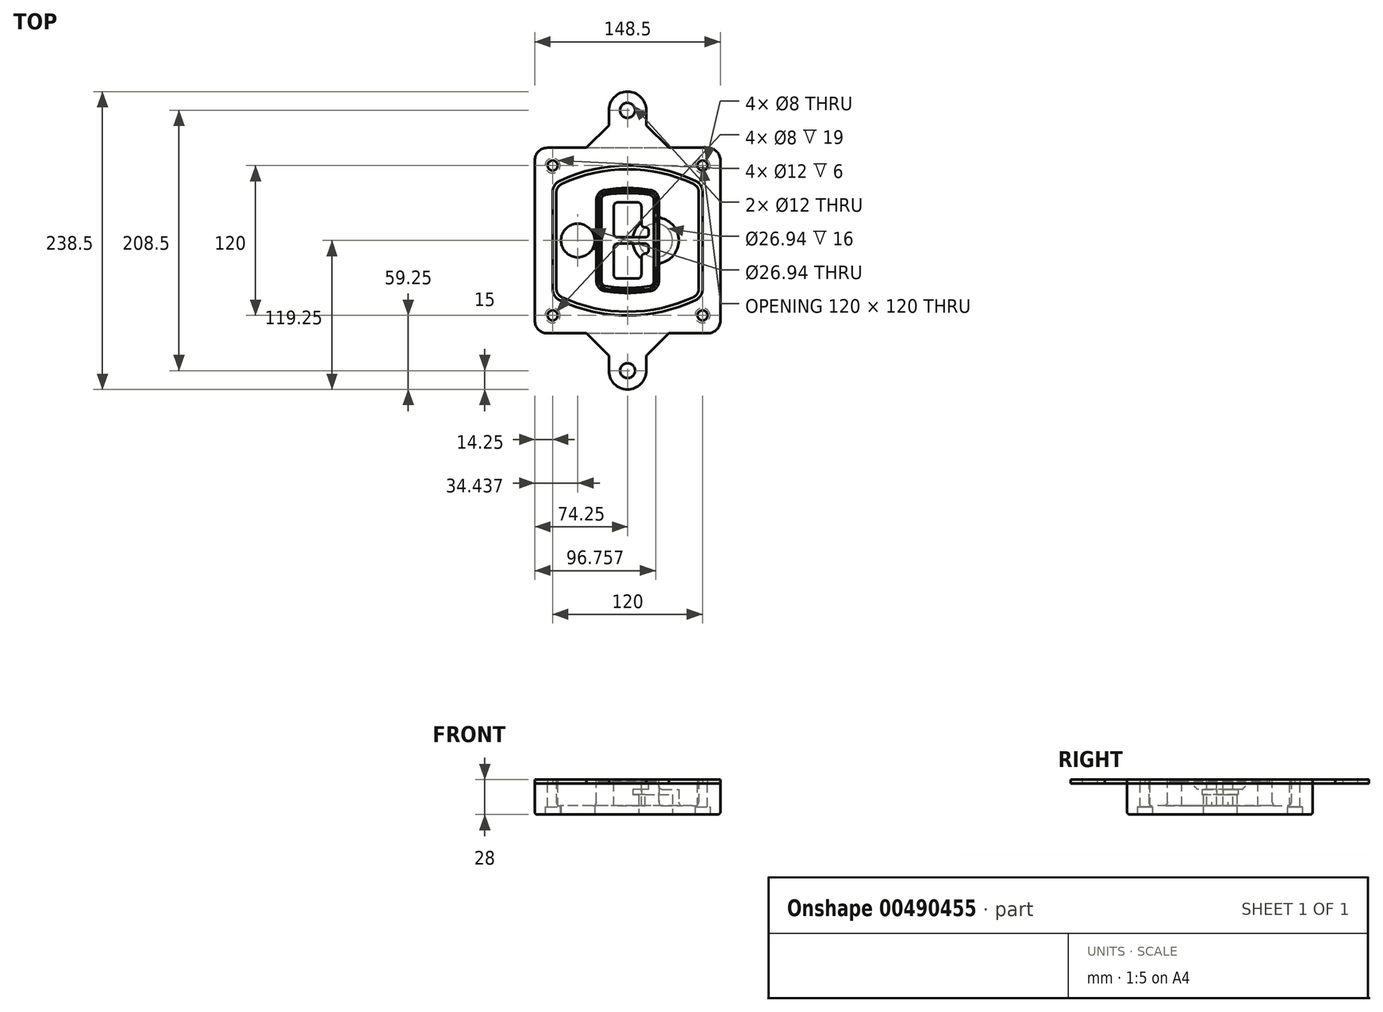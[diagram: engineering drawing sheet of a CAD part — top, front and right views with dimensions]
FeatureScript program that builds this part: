
annotation { "Feature Type Name" : "Feature", "Feature Type Description" : "" }
export const myFeature = defineFeature(function(context is Context, id is Id, definition is map)
    precondition{}
    {
        {
            var Q0;
            Q0=qCreatedBy(makeId("Top.planeOp"),FACE);
            var sketch = newSketch(context, id + "F0", { "sketchPlane" : qUnion([Q0])});
            skPoint(sketch, "E0.rect.middle", {"position": v(0, 0) * mm});
            skLineSegment(sketch, "E1.bottom", {"start": v(-64.25, -74.25) * mm, "end": v(64.25, -74.25) * mm});
            skLineSegment(sketch, "E1.top", {"start": v(-64.25, 74.25) * mm, "end": v(64.25, 74.25) * mm});
            skLineSegment(sketch, "E1.left", {"start": v(-74.25, -64.25) * mm, "end": v(-74.25, 64.25) * mm});
            skLineSegment(sketch, "E1.right", {"start": v(74.25, -64.25) * mm, "end": v(74.25, 64.25) * mm});
            skLineSegment(sketch, "E2", {"start": v(-74.25, 74.25) * mm, "end": v(74.25, -74.25) * mm, "construction": true});
            skLineSegment(sketch, "E3", {"start": v(74.25, 74.25) * mm, "end": v(-74.25, -74.25) * mm, "construction": true});
            skCircle(sketch, "E4", {"center": v(-60, 60) * mm, "radius": 4 * mm});
            skCircle(sketch, "E5", {"center": v(60, 60) * mm, "radius": 4 * mm});
            skCircle(sketch, "E6", {"center": v(60, -60) * mm, "radius": 4 * mm});
            skCircle(sketch, "E7", {"center": v(-60, -60) * mm, "radius": 4 * mm});
            skLineSegment(sketch, "E8", {"start": v(-60, 60) * mm, "end": v(60, 60) * mm, "construction": true});
            skLineSegment(sketch, "E9", {"start": v(60, 60) * mm, "end": v(60, -60) * mm, "construction": true});
            skLineSegment(sketch, "E10", {"start": v(60, -60) * mm, "end": v(-60, -60) * mm, "construction": true});
            skLineSegment(sketch, "E11", {"start": v(-60, -60) * mm, "end": v(-60, 60) * mm, "construction": true});
            skLineSegment(sketch, "E12", {"start": v(-60, 38.83) * mm, "end": v(-60, -38.83) * mm});
            skLineSegment(sketch, "E13", {"start": v(60, 38.83) * mm, "end": v(60, -38.83) * mm});
            skArc(sketch, "E14", {"start": v(54.26, 47.88) * mm, "mid": v(0, 60) * mm, "end": v(-54.26, 47.88) * mm});
            skArc(sketch, "E15", {"start": v(-54.26, -47.88) * mm, "mid": v(0, -60) * mm, "end": v(54.26, -47.88) * mm});
            skLineSegment(sketch, "E16", {"start": v(-60, 0) * mm, "end": v(60, 0) * mm, "construction": true});
            skPoint(sketch, "E17.visualSharp", {"position": v(-60, -45) * mm});
            skArc(sketch, "E17.filletArc", {"start": v(-60, -38.83) * mm, "mid": v(-58.44, -44.2) * mm, "end": v(-54.26, -47.88) * mm});
            skPoint(sketch, "E18.visualSharp", {"position": v(-60, 45) * mm});
            skArc(sketch, "E18.filletArc", {"start": v(-54.26, 47.88) * mm, "mid": v(-58.44, 44.2) * mm, "end": v(-60, 38.83) * mm});
            skPoint(sketch, "E19.visualSharp", {"position": v(60, 45) * mm});
            skArc(sketch, "E19.filletArc", {"start": v(60, 38.83) * mm, "mid": v(58.44, 44.2) * mm, "end": v(54.26, 47.88) * mm});
            skPoint(sketch, "E20.visualSharp", {"position": v(60, -45) * mm});
            skArc(sketch, "E20.filletArc", {"start": v(54.26, -47.88) * mm, "mid": v(58.44, -44.2) * mm, "end": v(60, -38.83) * mm});
            skPoint(sketch, "E21.visualSharp", {"position": v(-74.25, 74.25) * mm});
            skArc(sketch, "E21.filletArc", {"start": v(-64.25, 74.25) * mm, "mid": v(-71.32, 71.32) * mm, "end": v(-74.25, 64.25) * mm});
            skPoint(sketch, "E22.visualSharp", {"position": v(74.25, 74.25) * mm});
            skArc(sketch, "E22.filletArc", {"start": v(74.25, 64.25) * mm, "mid": v(71.32, 71.32) * mm, "end": v(64.25, 74.25) * mm});
            skPoint(sketch, "E23.visualSharp", {"position": v(74.25, -74.25) * mm});
            skArc(sketch, "E23.filletArc", {"start": v(64.25, -74.25) * mm, "mid": v(71.32, -71.32) * mm, "end": v(74.25, -64.25) * mm});
            skPoint(sketch, "E24.visualSharp", {"position": v(-74.25, -74.25) * mm});
            skArc(sketch, "E24.filletArc", {"start": v(-74.25, -64.25) * mm, "mid": v(-71.32, -71.32) * mm, "end": v(-64.25, -74.25) * mm});
            skArc(sketch, "E25.0", {"start": v(57, 38.83) * mm, "mid": v(55.9, 42.58) * mm, "end": v(52.98, 45.17) * mm});
            skLineSegment(sketch, "E25.1", {"start": v(57, 38.83) * mm, "end": v(57, -38.83) * mm});
            skArc(sketch, "E25.2", {"start": v(52.98, -45.17) * mm, "mid": v(55.9, -42.58) * mm, "end": v(57, -38.83) * mm});
            skArc(sketch, "E25.3", {"start": v(-52.98, -45.17) * mm, "mid": v(0, -57) * mm, "end": v(52.98, -45.17) * mm});
            skArc(sketch, "E25.4", {"start": v(-57, -38.83) * mm, "mid": v(-55.9, -42.58) * mm, "end": v(-52.98, -45.17) * mm});
            skArc(sketch, "E25.5", {"start": v(52.98, 45.17) * mm, "mid": v(0, 57) * mm, "end": v(-52.98, 45.17) * mm});
            skLineSegment(sketch, "E25.6", {"start": v(-57, 38.83) * mm, "end": v(-57, -38.83) * mm});
            skArc(sketch, "E25.7", {"start": v(-52.98, 45.17) * mm, "mid": v(-55.9, 42.58) * mm, "end": v(-57, 38.83) * mm});
            skArc(sketch, "E26.0", {"start": v(-55.96, 51.5) * mm, "mid": v(-61.82, 46.33) * mm, "end": v(-64, 38.83) * mm});
            skArc(sketch, "E26.1", {"start": v(55.96, 51.5) * mm, "mid": v(0, 64) * mm, "end": v(-55.96, 51.5) * mm});
            skArc(sketch, "E26.2", {"start": v(64, 38.83) * mm, "mid": v(61.82, 46.33) * mm, "end": v(55.96, 51.5) * mm});
            skLineSegment(sketch, "E26.3", {"start": v(64, 38.83) * mm, "end": v(64, -38.83) * mm});
            skArc(sketch, "E26.4", {"start": v(55.96, -51.5) * mm, "mid": v(61.82, -46.33) * mm, "end": v(64, -38.83) * mm});
            skLineSegment(sketch, "E26.5", {"start": v(-64, 38.83) * mm, "end": v(-64, -38.83) * mm});
            skArc(sketch, "E26.6", {"start": v(-55.96, -51.5) * mm, "mid": v(0, -64) * mm, "end": v(55.96, -51.5) * mm});
            skArc(sketch, "E26.7", {"start": v(-64, -38.83) * mm, "mid": v(-61.82, -46.33) * mm, "end": v(-55.96, -51.5) * mm});
            skSolve(sketch);
        }
        {
            var Q0;
            Q0=makeQuery(id+"F0.imprint","IMPRINT",FACE,{"disambiguationData":[TD([[makeQuery(id+"F0.imprint","IMPRINT",EDGE,{"derivedFrom":sQuery(id+"F0.wireOp",EDGE,"E1.bottom")}),1.0]])]});
            var Q1;
            Q1=makeQuery(id+"F0.imprint","IMPRINT",FACE,{"disambiguationData":[TD([[makeQuery(id+"F0.imprint","IMPRINT",EDGE,{"derivedFrom":sQuery(id+"F0.wireOp",EDGE,"E12")}),1.0]])]});
            var Q2;
            Q2=makeQuery(id+"F0.imprint","IMPRINT",FACE,{"disambiguationData":[TD([[makeQuery(id+"F0.imprint","IMPRINT",EDGE,{"derivedFrom":sQuery(id+"F0.wireOp",EDGE,"E25.0")}),1.0]])]});
            var Q3;
            Q3=makeQuery(id+"F0.imprint","IMPRINT",FACE,{"disambiguationData":[TD([[makeQuery(id+"F0.imprint","IMPRINT",EDGE,{"derivedFrom":sQuery(id+"F0.wireOp",EDGE,"E12")}),-1.0]])]});
            extrude(context, id + "F1", {"entities" : qUnion([Q0, Q1, Q2, Q3]), "oppositeDirection" : true, "depth" : 25 * mm});
        }
        {
            var Q0;
            Q0=makeQuery(id+"F0.imprint","IMPRINT",FACE,{"disambiguationData":[TD([[makeQuery(id+"F0.imprint","IMPRINT",EDGE,{"derivedFrom":sQuery(id+"F0.wireOp",EDGE,"E12")}),1.0]])]});
            extrude(context, id + "F2", {"entities" : qUnion([Q0]), "operationType" : NewBodyOperationType.ADD, "depth" : 3 * mm});
        }
        {
            var Q0;
            Q0=makeQuery(id+"F0.imprint","IMPRINT",FACE,{"disambiguationData":[TD([[makeQuery(id+"F0.imprint","IMPRINT",EDGE,{"derivedFrom":sQuery(id+"F0.wireOp",EDGE,"E25.0")}),1.0]])]});
            extrude(context, id + "F3", {"entities" : qUnion([Q0]), "operationType" : NewBodyOperationType.REMOVE, "oppositeDirection" : true, "depth" : 18 * mm});
        }
        {
            var Q0;
            Q0=makeQuery(id+"F2.opExtrude","CAP_FACE",FACE,{"disambiguationData":[OSD([sQuery(id+"F0.wireOp",EDGE,"E12"),sQuery(id+"F0.wireOp",EDGE,"E13"),sQuery(id+"F0.wireOp",EDGE,"E14"),sQuery(id+"F0.wireOp",EDGE,"E15"),sQuery(id+"F0.wireOp",EDGE,"E17.filletArc"),sQuery(id+"F0.wireOp",EDGE,"E18.filletArc"),sQuery(id+"F0.wireOp",EDGE,"E19.filletArc"),sQuery(id+"F0.wireOp",EDGE,"E20.filletArc"),sQuery(id+"F0.wireOp",EDGE,"E25.0"),sQuery(id+"F0.wireOp",EDGE,"E25.1"),sQuery(id+"F0.wireOp",EDGE,"E25.2"),sQuery(id+"F0.wireOp",EDGE,"E25.3"),sQuery(id+"F0.wireOp",EDGE,"E25.4"),sQuery(id+"F0.wireOp",EDGE,"E25.5"),sQuery(id+"F0.wireOp",EDGE,"E25.6"),sQuery(id+"F0.wireOp",EDGE,"E25.7")])],"isStart":false});
            var sketch = newSketch(context, id + "F4", { "sketchPlane" : qUnion([Q0])});
            skArc(sketch, "E27.0", {"start": v(-18.34, -40.45) * mm, "mid": v(0, -42) * mm, "end": v(18.34, -40.45) * mm});
            skArc(sketch, "E28.0", {"start": v(18.34, 40.45) * mm, "mid": v(0, 42) * mm, "end": v(-18.34, 40.45) * mm});
            skLineSegment(sketch, "E29", {"start": v(-25, 32.57) * mm, "end": v(-25, -32.57) * mm});
            skLineSegment(sketch, "E30", {"start": v(25, 32.57) * mm, "end": v(25, -32.57) * mm});
            skLineSegment(sketch, "E31", {"start": v(-25, 39.1) * mm, "end": v(25, 39.1) * mm, "construction": true});
            skLineSegment(sketch, "E32", {"start": v(-25, -39.1) * mm, "end": v(25, -39.1) * mm, "construction": true});
            skPoint(sketch, "E33.visualSharp", {"position": v(-25, 39.1) * mm});
            skArc(sketch, "E33.filletArc", {"start": v(-18.34, 40.45) * mm, "mid": v(-23.11, 37.73) * mm, "end": v(-25, 32.57) * mm});
            skPoint(sketch, "E34.visualSharp", {"position": v(25, 39.1) * mm});
            skArc(sketch, "E34.filletArc", {"start": v(25, 32.57) * mm, "mid": v(23.11, 37.73) * mm, "end": v(18.34, 40.45) * mm});
            skPoint(sketch, "E35.visualSharp", {"position": v(25, -39.1) * mm});
            skArc(sketch, "E35.filletArc", {"start": v(18.34, -40.45) * mm, "mid": v(23.11, -37.73) * mm, "end": v(25, -32.57) * mm});
            skPoint(sketch, "E36.visualSharp", {"position": v(-25, -39.1) * mm});
            skArc(sketch, "E36.filletArc", {"start": v(-25, -32.57) * mm, "mid": v(-23.11, -37.73) * mm, "end": v(-18.34, -40.45) * mm});
            skArc(sketch, "E37.0", {"start": v(52.98, 45.17) * mm, "mid": v(0, 57) * mm, "end": v(-52.98, 45.17) * mm});
            skArc(sketch, "E37.1", {"start": v(-52.98, 45.17) * mm, "mid": v(-55.9, 42.58) * mm, "end": v(-57, 38.83) * mm});
            skLineSegment(sketch, "E37.2", {"start": v(-57, 38.83) * mm, "end": v(-57, -38.83) * mm});
            skArc(sketch, "E37.3", {"start": v(-57, -38.83) * mm, "mid": v(-55.9, -42.58) * mm, "end": v(-52.98, -45.17) * mm});
            skArc(sketch, "E37.4", {"start": v(-52.98, -45.17) * mm, "mid": v(0, -57) * mm, "end": v(52.98, -45.17) * mm});
            skArc(sketch, "E37.5", {"start": v(52.98, -45.17) * mm, "mid": v(55.9, -42.58) * mm, "end": v(57, -38.83) * mm});
            skLineSegment(sketch, "E37.6", {"start": v(57, 38.83) * mm, "end": v(57, -38.83) * mm});
            skArc(sketch, "E37.7", {"start": v(57, 38.83) * mm, "mid": v(55.9, 42.58) * mm, "end": v(52.98, 45.17) * mm});
            skLineSegment(sketch, "E38.0", {"start": v(23, 32.57) * mm, "end": v(23, -32.57) * mm});
            skArc(sketch, "E38.1", {"start": v(18, -38.48) * mm, "mid": v(21.58, -36.44) * mm, "end": v(23, -32.57) * mm});
            skArc(sketch, "E38.2", {"start": v(-18, -38.48) * mm, "mid": v(0, -40) * mm, "end": v(18, -38.48) * mm});
            skArc(sketch, "E38.3", {"start": v(-23, -32.57) * mm, "mid": v(-21.58, -36.44) * mm, "end": v(-18, -38.48) * mm});
            skLineSegment(sketch, "E38.4", {"start": v(-23, 32.57) * mm, "end": v(-23, -32.57) * mm});
            skArc(sketch, "E38.5", {"start": v(23, 32.57) * mm, "mid": v(21.58, 36.44) * mm, "end": v(18, 38.48) * mm});
            skArc(sketch, "E38.6", {"start": v(-18, 38.48) * mm, "mid": v(-21.58, 36.44) * mm, "end": v(-23, 32.57) * mm});
            skArc(sketch, "E38.7", {"start": v(18, 38.48) * mm, "mid": v(0, 40) * mm, "end": v(-18, 38.48) * mm});
            skArc(sketch, "E39.0", {"start": v(21, 32.57) * mm, "mid": v(20.06, 35.15) * mm, "end": v(17.67, 36.5) * mm});
            skLineSegment(sketch, "E39.1", {"start": v(21, 32.57) * mm, "end": v(21, -32.57) * mm});
            skArc(sketch, "E39.2", {"start": v(17.67, -36.5) * mm, "mid": v(20.06, -35.15) * mm, "end": v(21, -32.57) * mm});
            skArc(sketch, "E39.3", {"start": v(-17.67, -36.5) * mm, "mid": v(0, -38) * mm, "end": v(17.67, -36.5) * mm});
            skArc(sketch, "E39.4", {"start": v(-21, -32.57) * mm, "mid": v(-20.06, -35.15) * mm, "end": v(-17.67, -36.5) * mm});
            skArc(sketch, "E39.5", {"start": v(17.67, 36.5) * mm, "mid": v(0, 38) * mm, "end": v(-17.67, 36.5) * mm});
            skLineSegment(sketch, "E39.6", {"start": v(-21, 32.57) * mm, "end": v(-21, -32.57) * mm});
            skArc(sketch, "E39.7", {"start": v(-17.67, 36.5) * mm, "mid": v(-20.06, 35.15) * mm, "end": v(-21, 32.57) * mm});
            skLineSegment(sketch, "E40", {"start": v(-25, 0) * mm, "end": v(25, 0) * mm, "construction": true});
            skLineSegment(sketch, "E41", {"start": v(-11, 5.5) * mm, "end": v(-11, 27.5) * mm});
            skLineSegment(sketch, "E42", {"start": v(-8, 30.5) * mm, "end": v(8, 30.5) * mm});
            skLineSegment(sketch, "E43", {"start": v(11, 27.5) * mm, "end": v(11, 13.5) * mm});
            skLineSegment(sketch, "E44", {"start": v(14, 10.5) * mm, "end": v(14, 10.5) * mm});
            skLineSegment(sketch, "E45", {"start": v(17, 7.5) * mm, "end": v(17, 5.5) * mm});
            skLineSegment(sketch, "E46", {"start": v(14, 2.5) * mm, "end": v(-8, 2.5) * mm});
            skPoint(sketch, "E47.visualSharp", {"position": v(-11, 30.5) * mm});
            skArc(sketch, "E47.filletArc", {"start": v(-8, 30.5) * mm, "mid": v(-10.12, 29.62) * mm, "end": v(-11, 27.5) * mm});
            skPoint(sketch, "E48.visualSharp", {"position": v(11, 30.5) * mm});
            skArc(sketch, "E48.filletArc", {"start": v(11, 27.5) * mm, "mid": v(10.12, 29.62) * mm, "end": v(8, 30.5) * mm});
            skPoint(sketch, "E49.visualSharp", {"position": v(11, 10.5) * mm});
            skArc(sketch, "E49.filletArc", {"start": v(11, 13.5) * mm, "mid": v(11.88, 11.38) * mm, "end": v(14, 10.5) * mm});
            skPoint(sketch, "E50.visualSharp", {"position": v(17, 10.5) * mm});
            skArc(sketch, "E50.filletArc", {"start": v(17, 7.5) * mm, "mid": v(16.12, 9.62) * mm, "end": v(14, 10.5) * mm});
            skPoint(sketch, "E51.visualSharp", {"position": v(17, 2.5) * mm});
            skArc(sketch, "E51.filletArc", {"start": v(14, 2.5) * mm, "mid": v(16.12, 3.38) * mm, "end": v(17, 5.5) * mm});
            skPoint(sketch, "E52.visualSharp", {"position": v(-11, 2.5) * mm});
            skArc(sketch, "E52.filletArc", {"start": v(-11, 5.5) * mm, "mid": v(-10.12, 3.38) * mm, "end": v(-8, 2.5) * mm});
            skLineSegment(sketch, "E53.0.MirrorCS", {"start": v(14, -2.5) * mm, "end": v(-8, -2.5) * mm});
            skArc(sketch, "E54.0.MirrorCS", {"start": v(-11, -5.5) * mm, "mid": v(-10.12, -3.38) * mm, "end": v(-8, -2.5) * mm});
            skLineSegment(sketch, "E55.0.MirrorCS", {"start": v(-11, -5.5) * mm, "end": v(-11, -27.5) * mm});
            skArc(sketch, "E56.0.MirrorCS", {"start": v(-8, -30.5) * mm, "mid": v(-10.12, -29.62) * mm, "end": v(-11, -27.5) * mm});
            skLineSegment(sketch, "E57.0.MirrorCS", {"start": v(-8, -30.5) * mm, "end": v(8, -30.5) * mm});
            skArc(sketch, "E58.0.MirrorCS", {"start": v(11, -27.5) * mm, "mid": v(10.12, -29.62) * mm, "end": v(8, -30.5) * mm});
            skLineSegment(sketch, "E59.0.MirrorCS", {"start": v(11, -27.5) * mm, "end": v(11, -13.5) * mm});
            skArc(sketch, "E60.0.MirrorCS", {"start": v(11, -13.5) * mm, "mid": v(11.88, -11.38) * mm, "end": v(14, -10.5) * mm});
            skArc(sketch, "E61.0.MirrorCS", {"start": v(17, -7.5) * mm, "mid": v(16.12, -9.62) * mm, "end": v(14, -10.5) * mm});
            skLineSegment(sketch, "E62.0.MirrorCS", {"start": v(17, -7.5) * mm, "end": v(17, -5.5) * mm});
            skArc(sketch, "E63.0.MirrorCS", {"start": v(14, -2.5) * mm, "mid": v(16.12, -3.38) * mm, "end": v(17, -5.5) * mm});
            skSolve(sketch);
        }
        {
            var Q0;
            Q0=makeQuery(id+"F4.imprint","IMPRINT",FACE,{"disambiguationData":[TD([[makeQuery(id+"F4.imprint","IMPRINT",EDGE,{"derivedFrom":sQuery(id+"F4.wireOp",EDGE,"E27.0")}),1.0]])]});
            var Q1;
            Q1=makeQuery(id+"F4.imprint","IMPRINT",FACE,{"disambiguationData":[TD([[makeQuery(id+"F4.imprint","IMPRINT",EDGE,{"derivedFrom":sQuery(id+"F4.wireOp",EDGE,"E38.0")}),-1.0]])]});
            var Q2;
            Q2=makeQuery(id+"F4.imprint","IMPRINT",FACE,{"disambiguationData":[TD([[makeQuery(id+"F4.imprint","IMPRINT",EDGE,{"derivedFrom":sQuery(id+"F4.wireOp",EDGE,"E39.0")}),1.0]])]});
            extrude(context, id + "F5", {"entities" : qUnion([Q0, Q1, Q2]), "operationType" : NewBodyOperationType.ADD, "endBound" : BoundingType.UP_TO_NEXT, "oppositeDirection" : true, "depth" : 25 * mm});
        }
        {
            var Q0;
            Q0=makeQuery(id+"F4.imprint","IMPRINT",FACE,{"disambiguationData":[TD([[makeQuery(id+"F4.imprint","IMPRINT",EDGE,{"derivedFrom":sQuery(id+"F4.wireOp",EDGE,"E38.0")}),-1.0]])]});
            extrude(context, id + "F6", {"entities" : qUnion([Q0]), "operationType" : NewBodyOperationType.REMOVE, "oppositeDirection" : true, "depth" : 2 * mm});
        }
        {
            var Q0;
            Q0=makeQuery(id+"F1.opExtrude","CAP_FACE",FACE,{"disambiguationData":[OSD([sQuery(id+"F0.wireOp",EDGE,"E1.bottom"),sQuery(id+"F0.wireOp",EDGE,"E1.top"),sQuery(id+"F0.wireOp",EDGE,"E1.left"),sQuery(id+"F0.wireOp",EDGE,"E1.right"),sQuery(id+"F0.wireOp",EDGE,"E4"),sQuery(id+"F0.wireOp",EDGE,"E5"),sQuery(id+"F0.wireOp",EDGE,"E6"),sQuery(id+"F0.wireOp",EDGE,"E7"),sQuery(id+"F0.wireOp",EDGE,"E21.filletArc"),sQuery(id+"F0.wireOp",EDGE,"E22.filletArc"),sQuery(id+"F0.wireOp",EDGE,"E23.filletArc"),sQuery(id+"F0.wireOp",EDGE,"E24.filletArc")])],"isStart":false});
            var sketch = newSketch(context, id + "F7", { "sketchPlane" : qUnion([Q0])});
            skCircle(sketch, "E64", {"center": v(22.5, 0) * mm, "radius": 13.47 * mm});
            skCircle(sketch, "E65", {"center": v(-39.81, 0) * mm, "radius": 13.47 * mm});
            skLineSegment(sketch, "E66", {"start": v(74.25, 0) * mm, "end": v(-74.25, 0) * mm});
            skCircle(sketch, "E67", {"center": v(22.5, 0) * mm, "radius": 18.47 * mm});
            skCircle(sketch, "E68", {"center": v(60, -60) * mm, "radius": 6 * mm});
            skCircle(sketch, "E69", {"center": v(-60, -60) * mm, "radius": 6 * mm});
            skCircle(sketch, "E70", {"center": v(-60, 60) * mm, "radius": 6 * mm});
            skCircle(sketch, "E71", {"center": v(60, 60) * mm, "radius": 6 * mm});
            skSolve(sketch);
        }
        {
            var Q0;
            {var subQ1=sQuery(id+"F7.wireOp",EDGE,"E66");var subQ4=sQuery(id+"F7.wireOp",EDGE,"E64");var subQ6=makeQuery(id+"F7.imprint","INTERSECT",VERTEX,{"disambiguationData":[OD(0.0)],"derivedFrom":[subQ4,subQ1]});Q0=makeQuery(id+"F7.imprint","IMPRINT",FACE,{"disambiguationData":[TD([[makeQuery(id+"F7.imprint","IMPRINT",EDGE,{"disambiguationData":[TD([[subQ6,-1.0]])],"derivedFrom":subQ4}),-1.0]])]});}
            var Q1;
            {var subQ0=sQuery(id+"F7.wireOp",EDGE,"E66");var subQ1=sQuery(id+"F7.wireOp",EDGE,"E64");var subQ3=makeQuery(id+"F7.imprint","INTERSECT",VERTEX,{"disambiguationData":[OD(0.0)],"derivedFrom":[subQ1,subQ0]});Q1=makeQuery(id+"F7.imprint","IMPRINT",FACE,{"disambiguationData":[TD([[makeQuery(id+"F7.imprint","IMPRINT",EDGE,{"disambiguationData":[TD([[subQ3,-1.0]])],"derivedFrom":subQ1}),1.0]])]});}
            var Q2;
            {var subQ0=sQuery(id+"F7.wireOp",EDGE,"E66");var subQ1=sQuery(id+"F7.wireOp",EDGE,"E64");var subQ3=makeQuery(id+"F7.imprint","INTERSECT",VERTEX,{"disambiguationData":[OD(0.0)],"derivedFrom":[subQ1,subQ0]});Q2=makeQuery(id+"F7.imprint","IMPRINT",FACE,{"disambiguationData":[TD([[makeQuery(id+"F7.imprint","IMPRINT",EDGE,{"disambiguationData":[TD([[subQ3,1.0]])],"derivedFrom":subQ1}),1.0]])]});}
            var Q3;
            {var subQ1=sQuery(id+"F7.wireOp",EDGE,"E66");var subQ4=sQuery(id+"F7.wireOp",EDGE,"E64");var subQ6=makeQuery(id+"F7.imprint","INTERSECT",VERTEX,{"disambiguationData":[OD(0.0)],"derivedFrom":[subQ4,subQ1]});Q3=makeQuery(id+"F7.imprint","IMPRINT",FACE,{"disambiguationData":[TD([[makeQuery(id+"F7.imprint","IMPRINT",EDGE,{"disambiguationData":[TD([[subQ6,1.0]])],"derivedFrom":subQ4}),-1.0]])]});}
            extrude(context, id + "F8", {"entities" : qUnion([Q0, Q1, Q2, Q3]), "operationType" : NewBodyOperationType.ADD, "oppositeDirection" : true, "depth" : 20 * mm});
        }
        {
            var Q0;
            {var subQ0=sQuery(id+"F7.wireOp",EDGE,"E66");var subQ1=sQuery(id+"F7.wireOp",EDGE,"E64");var subQ3=makeQuery(id+"F7.imprint","INTERSECT",VERTEX,{"disambiguationData":[OD(0.0)],"derivedFrom":[subQ1,subQ0]});Q0=makeQuery(id+"F7.imprint","IMPRINT",FACE,{"disambiguationData":[TD([[makeQuery(id+"F7.imprint","IMPRINT",EDGE,{"disambiguationData":[TD([[subQ3,-1.0]])],"derivedFrom":subQ1}),1.0]])]});}
            var Q1;
            {var subQ0=sQuery(id+"F7.wireOp",EDGE,"E66");var subQ1=sQuery(id+"F7.wireOp",EDGE,"E64");var subQ3=makeQuery(id+"F7.imprint","INTERSECT",VERTEX,{"disambiguationData":[OD(0.0)],"derivedFrom":[subQ1,subQ0]});Q1=makeQuery(id+"F7.imprint","IMPRINT",FACE,{"disambiguationData":[TD([[makeQuery(id+"F7.imprint","IMPRINT",EDGE,{"disambiguationData":[TD([[subQ3,1.0]])],"derivedFrom":subQ1}),1.0]])]});}
            extrude(context, id + "F9", {"entities" : qUnion([Q0, Q1]), "operationType" : NewBodyOperationType.REMOVE, "oppositeDirection" : true, "depth" : 16 * mm});
        }
        {
            var Q0;
            {var subQ0=sQuery(id+"F7.wireOp",EDGE,"E66");var subQ1=sQuery(id+"F7.wireOp",EDGE,"E65");var subQ3=makeQuery(id+"F7.imprint","INTERSECT",VERTEX,{"disambiguationData":[OD(0.0)],"derivedFrom":[subQ1,subQ0]});Q0=makeQuery(id+"F7.imprint","IMPRINT",FACE,{"disambiguationData":[TD([[makeQuery(id+"F7.imprint","IMPRINT",EDGE,{"disambiguationData":[TD([[subQ3,-1.0]])],"derivedFrom":subQ1}),1.0]])]});}
            var Q1;
            {var subQ0=sQuery(id+"F7.wireOp",EDGE,"E66");var subQ1=sQuery(id+"F7.wireOp",EDGE,"E65");var subQ3=makeQuery(id+"F7.imprint","INTERSECT",VERTEX,{"disambiguationData":[OD(0.0)],"derivedFrom":[subQ1,subQ0]});Q1=makeQuery(id+"F7.imprint","IMPRINT",FACE,{"disambiguationData":[TD([[makeQuery(id+"F7.imprint","IMPRINT",EDGE,{"disambiguationData":[TD([[subQ3,1.0]])],"derivedFrom":subQ1}),1.0]])]});}
            extrude(context, id + "F10", {"entities" : qUnion([Q0, Q1]), "operationType" : NewBodyOperationType.REMOVE, "oppositeDirection" : true, "depth" : 25 * mm});
        }
        {
            var Q0;
            Q0=makeQuery(id+"F7.imprint","IMPRINT",FACE,{"disambiguationData":[TD([[makeQuery(id+"F7.imprint","IMPRINT",EDGE,{"derivedFrom":sQuery(id+"F7.wireOp",EDGE,"E68")}),1.0]])]});
            var Q1;
            Q1=makeQuery(id+"F7.imprint","IMPRINT",FACE,{"disambiguationData":[TD([[makeQuery(id+"F7.imprint","IMPRINT",EDGE,{"derivedFrom":makeQuery(id+"F1.opExtrude","CAP_EDGE",EDGE,{"disambiguationData":[OSD([sQuery(id+"F0.wireOp",EDGE,"E5")])],"isStart":false})}),-1.0]])]});
            var Q2;
            Q2=makeQuery(id+"F7.imprint","IMPRINT",FACE,{"disambiguationData":[TD([[makeQuery(id+"F7.imprint","IMPRINT",EDGE,{"derivedFrom":sQuery(id+"F7.wireOp",EDGE,"E69")}),1.0]])]});
            var Q3;
            Q3=makeQuery(id+"F7.imprint","IMPRINT",FACE,{"disambiguationData":[TD([[makeQuery(id+"F7.imprint","IMPRINT",EDGE,{"derivedFrom":makeQuery(id+"F1.opExtrude","CAP_EDGE",EDGE,{"disambiguationData":[OSD([sQuery(id+"F0.wireOp",EDGE,"E4")])],"isStart":false})}),-1.0]])]});
            var Q4;
            Q4=makeQuery(id+"F7.imprint","IMPRINT",FACE,{"disambiguationData":[TD([[makeQuery(id+"F7.imprint","IMPRINT",EDGE,{"derivedFrom":sQuery(id+"F7.wireOp",EDGE,"E70")}),1.0]])]});
            var Q5;
            Q5=makeQuery(id+"F7.imprint","IMPRINT",FACE,{"disambiguationData":[TD([[makeQuery(id+"F7.imprint","IMPRINT",EDGE,{"derivedFrom":makeQuery(id+"F1.opExtrude","CAP_EDGE",EDGE,{"disambiguationData":[OSD([sQuery(id+"F0.wireOp",EDGE,"E7")])],"isStart":false})}),-1.0]])]});
            var Q6;
            Q6=makeQuery(id+"F7.imprint","IMPRINT",FACE,{"disambiguationData":[TD([[makeQuery(id+"F7.imprint","IMPRINT",EDGE,{"derivedFrom":sQuery(id+"F7.wireOp",EDGE,"E71")}),1.0]])]});
            var Q7;
            Q7=makeQuery(id+"F7.imprint","IMPRINT",FACE,{"disambiguationData":[TD([[makeQuery(id+"F7.imprint","IMPRINT",EDGE,{"derivedFrom":makeQuery(id+"F1.opExtrude","CAP_EDGE",EDGE,{"disambiguationData":[OSD([sQuery(id+"F0.wireOp",EDGE,"E6")])],"isStart":false})}),-1.0]])]});
            extrude(context, id + "F11", {"entities" : qUnion([Q0, Q1, Q2, Q3, Q4, Q5, Q6, Q7]), "operationType" : NewBodyOperationType.REMOVE, "oppositeDirection" : true, "depth" : 6 * mm});
        }
        {
            var Q0;
            Q0=makeQuery(id+"F9.boolean.opBoolean","COPY",FACE,{"derivedFrom":makeQuery(id+"F9.opExtrude","CAP_FACE",FACE,{"disambiguationData":[OSD([sQuery(id+"F7.wireOp",EDGE,"E64")])],"isStart":false})});
            var sketch = newSketch(context, id + "F12", { "sketchPlane" : qUnion([Q0])});
            skArc(sketch, "E72.0", {"start": v(11, 14.45) * mm, "mid": v(6.45, 9.13) * mm, "end": v(4.2, 2.5) * mm});
            skArc(sketch, "E72.1", {"start": v(4.2, -2.5) * mm, "mid": v(6.45, -9.13) * mm, "end": v(11, -14.45) * mm});
            skLineSegment(sketch, "E73", {"start": v(4.2, -2.5) * mm, "end": v(14, -2.5) * mm});
            skLineSegment(sketch, "E74.0", {"start": v(14, 2.5) * mm, "end": v(4.2, 2.5) * mm});
            skArc(sketch, "E74.1", {"start": v(14, 2.5) * mm, "mid": v(16.12, 3.38) * mm, "end": v(17, 5.5) * mm});
            skLineSegment(sketch, "E74.2", {"start": v(17, 7.5) * mm, "end": v(17, 5.5) * mm});
            skArc(sketch, "E74.3", {"start": v(17, 7.5) * mm, "mid": v(16.12, 9.62) * mm, "end": v(14, 10.5) * mm});
            skArc(sketch, "E74.4", {"start": v(11, 13.5) * mm, "mid": v(11.88, 11.38) * mm, "end": v(14, 10.5) * mm});
            skLineSegment(sketch, "E74.5", {"start": v(11, 14.45) * mm, "end": v(11, 13.5) * mm});
            skLineSegment(sketch, "E74.7", {"start": v(14, -2.5) * mm, "end": v(4.2, -2.5) * mm});
            skArc(sketch, "E74.8", {"start": v(14, -2.5) * mm, "mid": v(16.12, -3.38) * mm, "end": v(17, -5.5) * mm});
            skLineSegment(sketch, "E74.9", {"start": v(17, -7.5) * mm, "end": v(17, -5.5) * mm});
            skArc(sketch, "E74.10", {"start": v(17, -7.5) * mm, "mid": v(16.12, -9.62) * mm, "end": v(14, -10.5) * mm});
            skArc(sketch, "E74.11", {"start": v(11, -13.5) * mm, "mid": v(11.88, -11.38) * mm, "end": v(14, -10.5) * mm});
            skLineSegment(sketch, "E74.12", {"start": v(11, -14.45) * mm, "end": v(11, -13.5) * mm});
            skPoint(sketch, "E75.orphan", {"position": v(11, -27.5) * mm});
            skPoint(sketch, "E76.orphan", {"position": v(-8, -2.5) * mm});
            skPoint(sketch, "E77.orphan", {"position": v(-8, 2.5) * mm});
            skPoint(sketch, "E78.orphan", {"position": v(11, 27.5) * mm});
            skSolve(sketch);
        }
        {
            var Q0;
            {var subQ7=sQuery(id+"F12.wireOp",EDGE,"E72.0");var subQ14=sQuery(id+"F12.wireOp",EDGE,"E72.1");var subQ16=sQuery(id+"F12.wireOp",EDGE,"E74.1");var subQ18=sQuery(id+"F12.wireOp",EDGE,"E74.8");Q0=qUnion([makeQuery(id+"F12.imprint","IMPRINT",FACE,{"disambiguationData":[TD([[makeQuery(id+"F12.imprint","IMPRINT",EDGE,{"derivedFrom":subQ7}),1.0]])]}),makeQuery(id+"F12.imprint","IMPRINT",FACE,{"disambiguationData":[TD([[makeQuery(id+"F12.imprint","IMPRINT",EDGE,{"derivedFrom":subQ14}),1.0]])]}),makeQuery(id+"F12.imprint","IMPRINT",FACE,{"disambiguationData":[TD([[makeQuery(id+"F12.imprint","IMPRINT",EDGE,{"derivedFrom":subQ16}),1.0]])]}),makeQuery(id+"F12.imprint","IMPRINT",FACE,{"disambiguationData":[TD([[makeQuery(id+"F12.imprint","IMPRINT",EDGE,{"derivedFrom":subQ18}),-1.0]])]})]);}
            var Q1;
            Q1=makeQuery(id+"F5.boolean.opBoolean","SPLIT",FACE,{"disambiguationData":[TD([makeQuery(id+"F5.opExtrude","SWEPT_FACE",FACE,{"disambiguationData":[OSD([sQuery(id+"F4.wireOp",EDGE,"E41")])]})])],"derivedFrom":makeQuery(id+"F3.boolean.opBoolean","COPY",FACE,{"derivedFrom":makeQuery(id+"F3.opExtrude","CAP_FACE",FACE,{"disambiguationData":[OSD([sQuery(id+"F0.wireOp",EDGE,"E25.0"),sQuery(id+"F0.wireOp",EDGE,"E25.1"),sQuery(id+"F0.wireOp",EDGE,"E25.2"),sQuery(id+"F0.wireOp",EDGE,"E25.3"),sQuery(id+"F0.wireOp",EDGE,"E25.4"),sQuery(id+"F0.wireOp",EDGE,"E25.5"),sQuery(id+"F0.wireOp",EDGE,"E25.6"),sQuery(id+"F0.wireOp",EDGE,"E25.7")])],"isStart":false})})});
            extrude(context, id + "F13", {"entities" : qUnion([Q0]), "operationType" : NewBodyOperationType.REMOVE, "endBound" : BoundingType.UP_TO_SURFACE, "endBoundEntityFace" : qUnion([Q1]), "depth" : 25 * mm});
        }
        {
            var Q0;
            Q0=makeQuery(id+"F3.boolean.opBoolean","COPY",EDGE,{"derivedFrom":makeQuery(id+"F3.opExtrude","CAP_EDGE",EDGE,{"disambiguationData":[OSD([sQuery(id+"F0.wireOp",EDGE,"E25.6")])],"isStart":false})});
            var Q1;
            Q1=makeQuery(id+"F8.boolean.opBoolean","INTERSECT",EDGE,{"derivedFrom":[makeQuery(id+"F5.opExtrude","SWEPT_FACE",FACE,{"disambiguationData":[OSD([sQuery(id+"F4.wireOp",EDGE,"E30")])]}),makeQuery(id+"F8.opExtrude","CAP_FACE",FACE,{"disambiguationData":[OSD([sQuery(id+"F7.wireOp",EDGE,"E67")])],"isStart":false})]});
            var Q2;
            Q2=makeQuery(id+"F8.boolean.opBoolean","INTERSECT",EDGE,{"disambiguationData":[OD(1.0)],"derivedFrom":[makeQuery(id+"F5.opExtrude","SWEPT_FACE",FACE,{"disambiguationData":[OSD([sQuery(id+"F4.wireOp",EDGE,"E30")])]}),makeQuery(id+"F8.opExtrude","SWEPT_FACE",FACE,{"disambiguationData":[OSD([sQuery(id+"F7.wireOp",EDGE,"E67")])]})]});
            var Q3;
            {var subQ0=sQuery(id+"F4.wireOp",EDGE,"E30");Q3=makeQuery(id+"F8.boolean.opBoolean","SPLIT",EDGE,{"disambiguationData":[TD([makeQuery(id+"F5.opExtrude","SWEPT_FACE",FACE,{"disambiguationData":[OSD([sQuery(id+"F4.wireOp",EDGE,"E35.filletArc")])]})])],"derivedFrom":makeQuery(id+"F5.opExtrude","CAP_EDGE",EDGE,{"disambiguationData":[OSD([subQ0])],"isStart":false})});}
            var Q4;
            {var subQ0=sQuery(id+"F0.wireOp",EDGE,"E25.7");var subQ1=sQuery(id+"F0.wireOp",EDGE,"E25.1");var subQ2=sQuery(id+"F0.wireOp",EDGE,"E25.6");var subQ3=sQuery(id+"F0.wireOp",EDGE,"E25.5");var subQ4=sQuery(id+"F0.wireOp",EDGE,"E25.4");var subQ5=sQuery(id+"F0.wireOp",EDGE,"E25.0");var subQ6=sQuery(id+"F0.wireOp",EDGE,"E25.2");var subQ7=sQuery(id+"F0.wireOp",EDGE,"E25.3");Q4=makeQuery(id+"F8.boolean.opBoolean","INTERSECT",EDGE,{"derivedFrom":[makeQuery(id+"F5.boolean.opBoolean","SPLIT",FACE,{"disambiguationData":[TD([makeQuery(id+"F2.opExtrude","SWEPT_FACE",FACE,{"disambiguationData":[OSD([subQ5])]})])],"derivedFrom":makeQuery(id+"F3.boolean.opBoolean","COPY",FACE,{"derivedFrom":makeQuery(id+"F3.opExtrude","CAP_FACE",FACE,{"disambiguationData":[OSD([subQ5,subQ1,subQ6,subQ7,subQ4,subQ3,subQ2,subQ0])],"isStart":false})})}),makeQuery(id+"F8.opExtrude","SWEPT_FACE",FACE,{"disambiguationData":[OSD([sQuery(id+"F7.wireOp",EDGE,"E67")])]})]});}
            var Q5;
            Q5=makeQuery(id+"F8.boolean.opBoolean","INTERSECT",EDGE,{"disambiguationData":[OD(0.0)],"derivedFrom":[makeQuery(id+"F5.opExtrude","SWEPT_FACE",FACE,{"disambiguationData":[OSD([sQuery(id+"F4.wireOp",EDGE,"E30")])]}),makeQuery(id+"F8.opExtrude","SWEPT_FACE",FACE,{"disambiguationData":[OSD([sQuery(id+"F7.wireOp",EDGE,"E67")])]})]});
            fillet(context, id + "F14", {"entities" : qUnion([Q0, Q1, Q2, Q3, Q4, Q5]), "radius" : 3 * mm, "tangentPropagation" : true, "allowEdgeOverflow" : false});
        }
        {
            var Q0;
            Q0=makeQuery(id+"F1.opExtrude","CAP_EDGE",EDGE,{"disambiguationData":[OSD([sQuery(id+"F0.wireOp",EDGE,"E1.bottom")])],"isStart":false});
            fillet(context, id + "F15", {"entities" : qUnion([Q0]), "radius" : 2 * mm, "tangentPropagation" : true, "allowEdgeOverflow" : false});
        }
        {
            var Q0;
            {var subQ0=sQuery(id+"F0.wireOp",EDGE,"E21.filletArc");var subQ1=sQuery(id+"F0.wireOp",EDGE,"E7");var subQ2=sQuery(id+"F0.wireOp",EDGE,"E6");var subQ3=sQuery(id+"F0.wireOp",EDGE,"E5");var subQ4=sQuery(id+"F0.wireOp",EDGE,"E4");var subQ5=sQuery(id+"F0.wireOp",EDGE,"E22.filletArc");var subQ6=sQuery(id+"F0.wireOp",EDGE,"E1.bottom");var subQ7=sQuery(id+"F0.wireOp",EDGE,"E1.right");var subQ8=sQuery(id+"F0.wireOp",EDGE,"E1.top");var subQ9=sQuery(id+"F0.wireOp",EDGE,"E1.left");var subQ10=sQuery(id+"F0.wireOp",EDGE,"E23.filletArc");var subQ11=sQuery(id+"F0.wireOp",EDGE,"E24.filletArc");Q0=makeQuery(id+"F2.boolean.opBoolean","SPLIT",FACE,{"disambiguationData":[TD([makeQuery(id+"F1.opExtrude","SWEPT_FACE",FACE,{"disambiguationData":[OSD([subQ6])]})])],"derivedFrom":makeQuery(id+"F1.opExtrude","CAP_FACE",FACE,{"disambiguationData":[OSD([subQ6,subQ8,subQ9,subQ7,subQ4,subQ3,subQ2,subQ1,subQ0,subQ5,subQ10,subQ11])],"isStart":true})});}
            var sketch = newSketch(context, id + "F16", { "sketchPlane" : qUnion([Q0])});
            skLineSegment(sketch, "E79", {"start": v(0, 74.25) * mm, "end": v(0, 104.25) * mm, "construction": true});
            skArc(sketch, "E80", {"start": v(15, 104.25) * mm, "mid": v(0, 119.25) * mm, "end": v(-15, 104.25) * mm});
            skLineSegment(sketch, "E81", {"start": v(15, 104.25) * mm, "end": v(15, 92.25) * mm});
            skLineSegment(sketch, "E82", {"start": v(-15, 104.25) * mm, "end": v(-15, 92.25) * mm});
            skLineSegment(sketch, "E83", {"start": v(-15, 92.25) * mm, "end": v(-33, 74.25) * mm});
            skLineSegment(sketch, "E84", {"start": v(15, 92.25) * mm, "end": v(33, 74.25) * mm});
            skCircle(sketch, "E85", {"center": v(0, 104.25) * mm, "radius": 6 * mm});
            skLineSegment(sketch, "E86", {"start": v(-74.25, 0) * mm, "end": v(74.25, 0) * mm, "construction": true});
            skLineSegment(sketch, "E87.MirrorCS", {"start": v(15, -104.25) * mm, "end": v(15, -92.25) * mm});
            skLineSegment(sketch, "E88.MirrorCS", {"start": v(-15, -104.25) * mm, "end": v(-15, -92.25) * mm});
            skLineSegment(sketch, "E89.MirrorCS", {"start": v(-15, -92.25) * mm, "end": v(-33, -74.25) * mm});
            skLineSegment(sketch, "E90.MirrorCS", {"start": v(15, -92.25) * mm, "end": v(33, -74.25) * mm});
            skLineSegment(sketch, "E91.MirrorCS", {"start": v(0, -74.25) * mm, "end": v(0, -104.25) * mm, "construction": true});
            skArc(sketch, "E92.MirrorCS", {"start": v(15, -104.25) * mm, "mid": v(0, -119.25) * mm, "end": v(-15, -104.25) * mm});
            skCircle(sketch, "E93.MirrorC", {"center": v(0, -104.25) * mm, "radius": 6 * mm});
            skSolve(sketch);
        }
        {
            var Q0;
            Q0=makeQuery(id+"F16.imprint","IMPRINT",FACE,{"disambiguationData":[TD([[makeQuery(id+"F16.imprint","IMPRINT",EDGE,{"derivedFrom":sQuery(id+"F16.wireOp",EDGE,"E80")}),1.0]])]});
            var Q1;
            Q1=makeQuery(id+"F16.imprint","IMPRINT",FACE,{"disambiguationData":[TD([[makeQuery(id+"F16.imprint","IMPRINT",EDGE,{"derivedFrom":makeQuery(id+"F1.opExtrude","CAP_EDGE",EDGE,{"disambiguationData":[OSD([sQuery(id+"F0.wireOp",EDGE,"E1.left")])],"isStart":true})}),-1.0]])]});
            var Q2;
            Q2=makeQuery(id+"F16.imprint","IMPRINT",FACE,{"disambiguationData":[TD([[makeQuery(id+"F16.imprint","IMPRINT",EDGE,{"derivedFrom":sQuery(id+"F16.wireOp",EDGE,"E87.MirrorCS")}),1.0]])]});
            var Q3;
            Q3=makeQuery(id+"F2.opExtrude","CAP_FACE",FACE,{"disambiguationData":[OSD([sQuery(id+"F0.wireOp",EDGE,"E12"),sQuery(id+"F0.wireOp",EDGE,"E13"),sQuery(id+"F0.wireOp",EDGE,"E14"),sQuery(id+"F0.wireOp",EDGE,"E15"),sQuery(id+"F0.wireOp",EDGE,"E17.filletArc"),sQuery(id+"F0.wireOp",EDGE,"E18.filletArc"),sQuery(id+"F0.wireOp",EDGE,"E19.filletArc"),sQuery(id+"F0.wireOp",EDGE,"E20.filletArc"),sQuery(id+"F0.wireOp",EDGE,"E25.0"),sQuery(id+"F0.wireOp",EDGE,"E25.1"),sQuery(id+"F0.wireOp",EDGE,"E25.2"),sQuery(id+"F0.wireOp",EDGE,"E25.3"),sQuery(id+"F0.wireOp",EDGE,"E25.4"),sQuery(id+"F0.wireOp",EDGE,"E25.5"),sQuery(id+"F0.wireOp",EDGE,"E25.6"),sQuery(id+"F0.wireOp",EDGE,"E25.7")])],"isStart":false});
            extrude(context, id + "F17", {"entities" : qUnion([Q0, Q1, Q2]), "endBound" : BoundingType.UP_TO_SURFACE, "endBoundEntityFace" : qUnion([Q3]), "depth" : 25 * mm});
        }
    });
